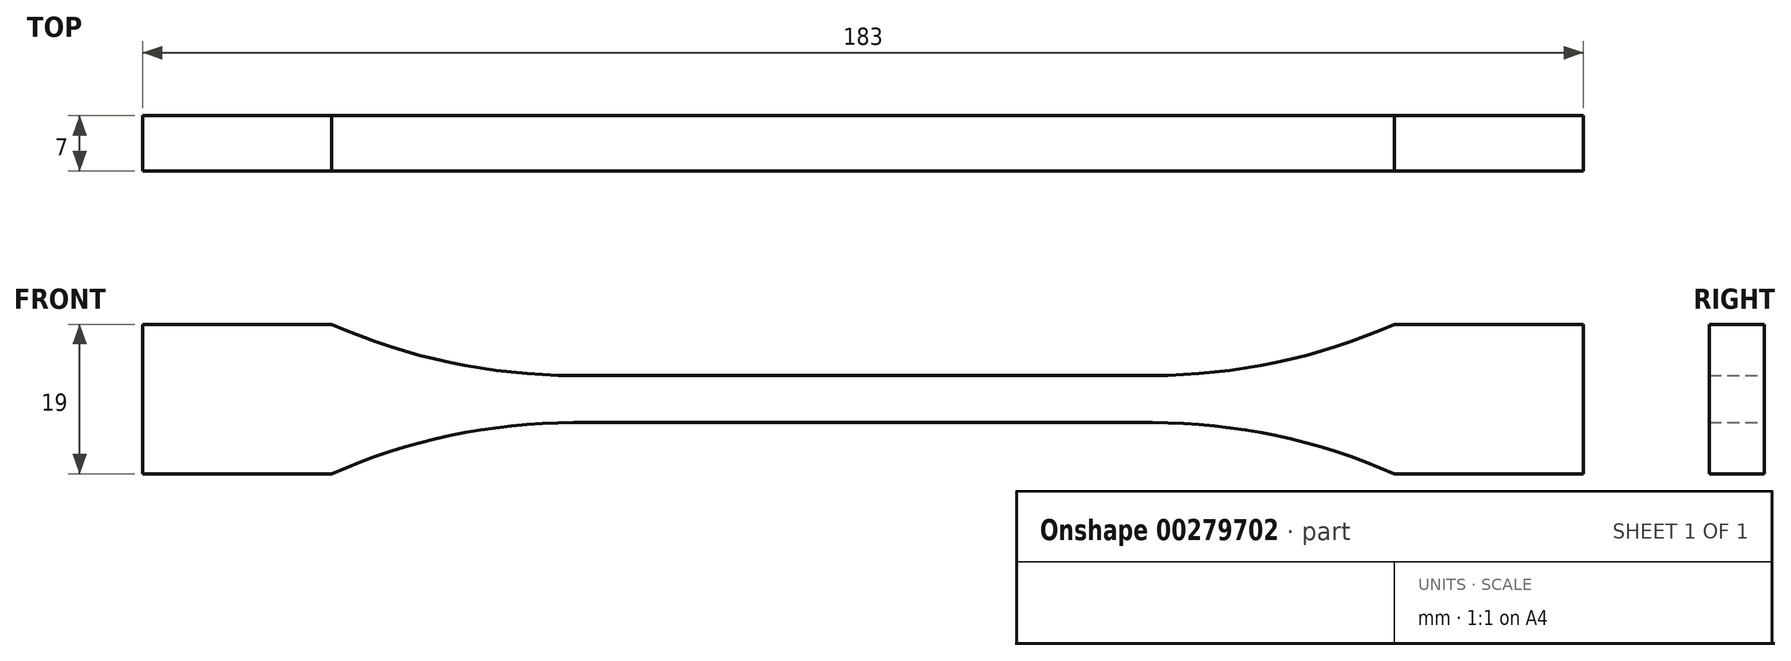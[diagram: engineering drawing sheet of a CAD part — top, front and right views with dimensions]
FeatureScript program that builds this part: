
annotation { "Feature Type Name" : "Feature", "Feature Type Description" : "" }
export const myFeature = defineFeature(function(context is Context, id is Id, definition is map)
    precondition{}
    {
        {
            var Q0;
            Q0=qCreatedBy(makeId("Front.planeOp"),FACE);
            var sketch = newSketch(context, id + "F0", { "sketchPlane" : qUnion([Q0])});
            skLineSegment(sketch, "E0", {"start": v(0, 3) * mm, "end": v(36.75, 3) * mm});
            skArc(sketch, "E1", {"start": v(36.75, 3) * mm, "mid": v(52.46, 4.64) * mm, "end": v(67.5, 9.5) * mm});
            skLineSegment(sketch, "E2", {"start": v(67.5, 9.5) * mm, "end": v(91.5, 9.5) * mm});
            skArc(sketch, "E3.MirrorCS", {"start": v(36.75, -3) * mm, "mid": v(52.46, -4.64) * mm, "end": v(67.5, -9.5) * mm});
            skLineSegment(sketch, "E4.MirrorCS", {"start": v(0, -3) * mm, "end": v(36.75, -3) * mm});
            skLineSegment(sketch, "E5.MirrorCS", {"start": v(67.5, -9.5) * mm, "end": v(91.5, -9.5) * mm});
            skLineSegment(sketch, "E6.MirrorCS", {"start": v(0, 3) * mm, "end": v(-36.75, 3) * mm});
            skArc(sketch, "E7.MirrorCS", {"start": v(-36.75, -3) * mm, "mid": v(-52.46, -4.64) * mm, "end": v(-67.5, -9.5) * mm});
            skArc(sketch, "E8.MirrorCS", {"start": v(-36.75, 3) * mm, "mid": v(-52.46, 4.64) * mm, "end": v(-67.5, 9.5) * mm});
            skLineSegment(sketch, "E9.MirrorCS", {"start": v(-67.5, 9.5) * mm, "end": v(-91.5, 9.5) * mm});
            skLineSegment(sketch, "E10.MirrorCS", {"start": v(0, -3) * mm, "end": v(-36.75, -3) * mm});
            skLineSegment(sketch, "E11.MirrorCS", {"start": v(-67.5, -9.5) * mm, "end": v(-91.5, -9.5) * mm});
            skLineSegment(sketch, "E12", {"start": v(-91.5, -9.5) * mm, "end": v(-91.5, 9.5) * mm});
            skLineSegment(sketch, "E13", {"start": v(91.5, -9.5) * mm, "end": v(91.5, 9.5) * mm});
            skSolve(sketch);
        }
        {
            var Q0;
            Q0=makeQuery(id+"F0.imprint","IMPRINT",FACE,{"disambiguationData":[TD([[makeQuery(id+"F0.imprint","IMPRINT",EDGE,{"derivedFrom":sQuery(id+"F0.wireOp",EDGE,"E0")}),-1.0]])]});
            extrude(context, id + "F1", {"entities" : qUnion([Q0]), "endBound" : BoundingType.SYMMETRIC, "depth" : 7 * mm});
        }
    });
